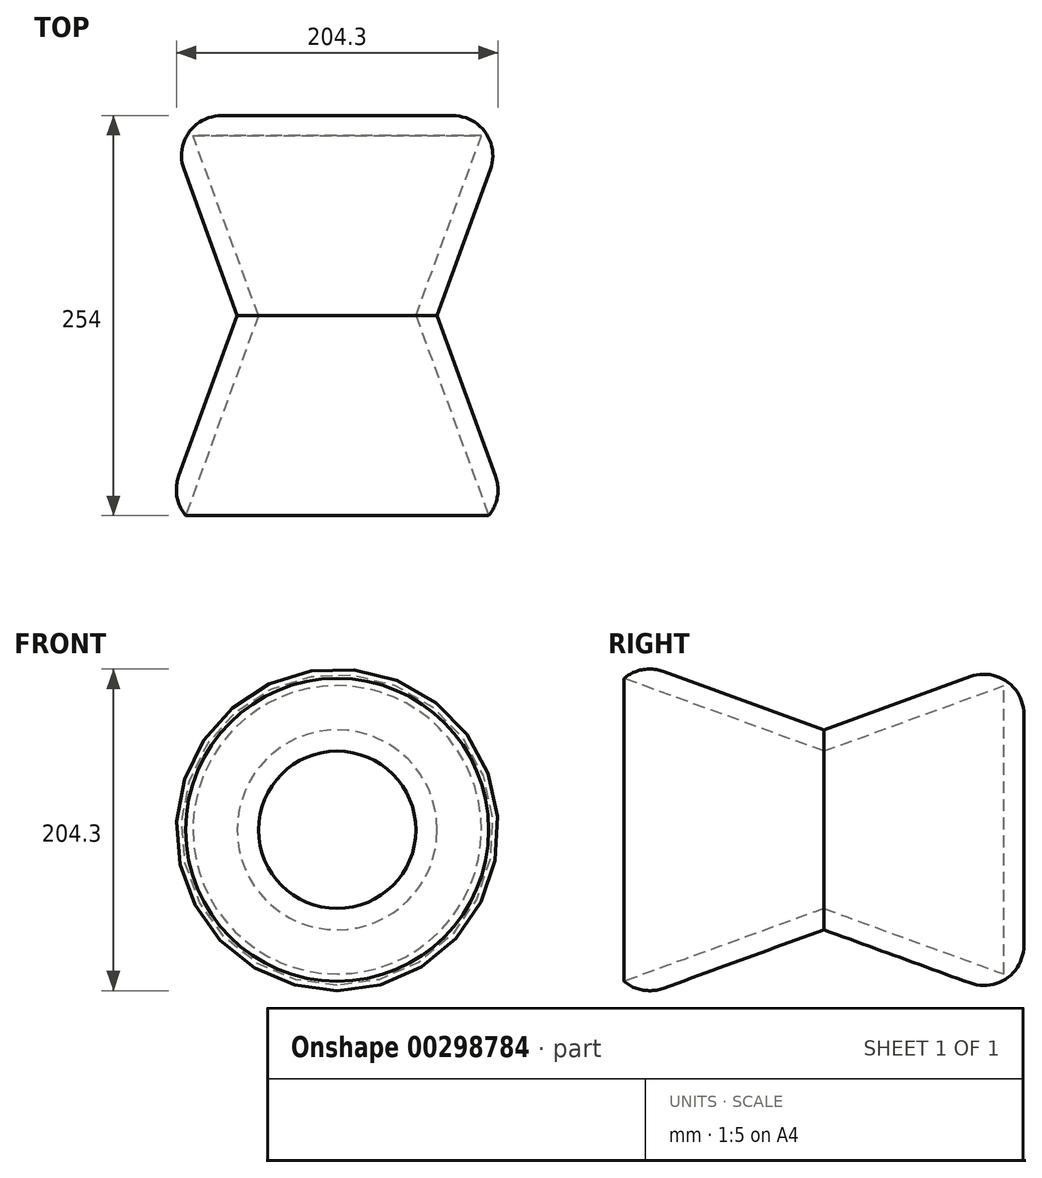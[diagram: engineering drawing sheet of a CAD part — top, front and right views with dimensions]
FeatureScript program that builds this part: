
annotation { "Feature Type Name" : "Feature", "Feature Type Description" : "" }
export const myFeature = defineFeature(function(context is Context, id is Id, definition is map)
    precondition{}
    {
        {
            var Q0;
            Q0=qCreatedBy(makeId("Front.planeOp"),FACE);
            var sketch = newSketch(context, id + "F0", { "sketchPlane" : qUnion([Q0])});
            skCircle(sketch, "E0", {"center": v(0, 0) * mm, "radius": 63.5 * mm});
            skSolve(sketch);
        }
        {
            var Q0;
            Q0=makeQuery(id+"F0.imprint","IMPRINT",FACE,{"disambiguationData":[TD([[makeQuery(id+"F0.imprint","IMPRINT",EDGE,{"derivedFrom":sQuery(id+"F0.wireOp",EDGE,"E0")}),1.0]])]});
            extrude(context, id + "F1", {"entities" : qUnion([Q0]), "endBound" : BoundingType.SYMMETRIC, "depth" : 254 * mm, "hasDraft" : true, "draftAngle" : 20 * degree});
        }
        {
            var Q0;
            Q0=makeQuery(id+"F1.opExtrude","CAP_FACE",FACE,{"disambiguationData":[OSD([sQuery(id+"F0.wireOp",EDGE,"E0")])],"isStart":false});
            shell(context, id + "F2", {"entities" : qUnion([Q0]), "thickness" : 12.7 * mm});
        }
        {
            var Q0;
            Q0=makeQuery(id+"F1.opExtrude","CAP_EDGE",EDGE,{"disambiguationData":[OSD([sQuery(id+"F0.wireOp",EDGE,"E0")])],"isStart":false});
            var Q1;
            Q1=makeQuery(id+"F1.opExtrude","CAP_EDGE",EDGE,{"disambiguationData":[OSD([sQuery(id+"F0.wireOp",EDGE,"E0")])],"isStart":true});
            fillet(context, id + "F3", {"entities" : qUnion([Q0, Q1]), "radius" : 25.4 * mm, "tangentPropagation" : true, "allowEdgeOverflow" : false});
        }
    });
